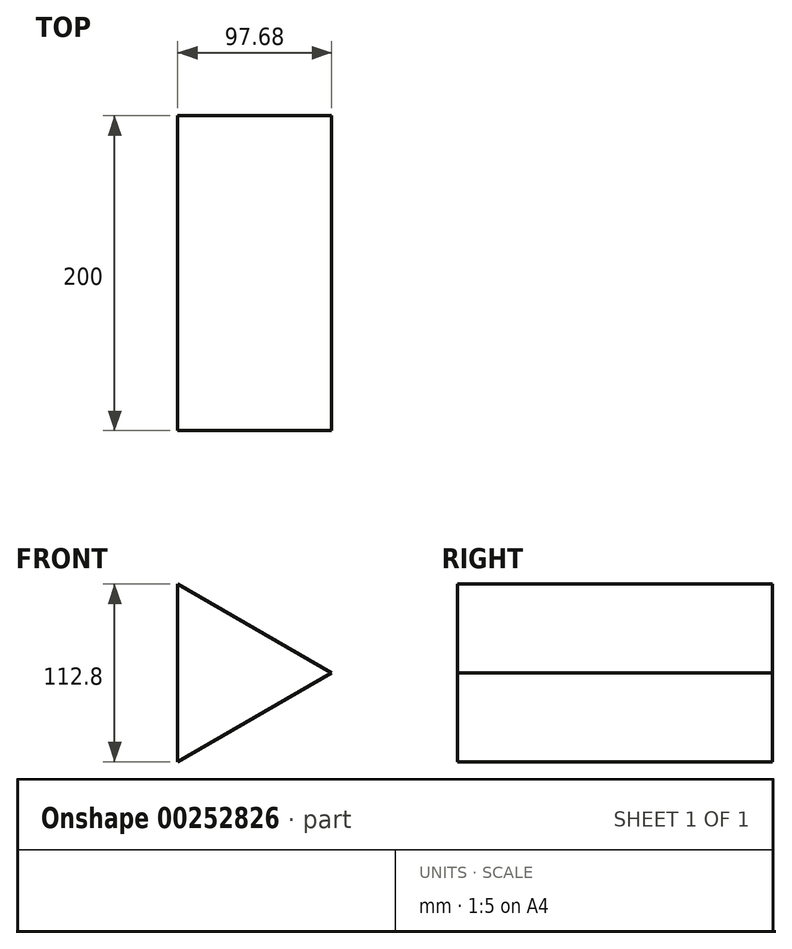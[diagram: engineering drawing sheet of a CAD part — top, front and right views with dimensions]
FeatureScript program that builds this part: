
annotation { "Feature Type Name" : "Feature", "Feature Type Description" : "" }
export const myFeature = defineFeature(function(context is Context, id is Id, definition is map)
    precondition{}
    {
        {
            var Q0;
            Q0=qCreatedBy(makeId("Front.planeOp"),FACE);
            var sketch = newSketch(context, id + "F0", { "sketchPlane" : qUnion([Q0])});
            skCircle(sketch, "E0.cCircle", {"center": v(0, 0) * mm, "radius": 65.12 * mm, "construction": true});
            skLineSegment(sketch, "E0.0", {"start": v(65.12, 0) * mm, "end": v(-32.56, -56.4) * mm});
            skLineSegment(sketch, "E0.1", {"start": v(-32.56, -56.4) * mm, "end": v(-32.56, 56.4) * mm});
            skLineSegment(sketch, "E0.2", {"start": v(-32.56, 56.4) * mm, "end": v(65.12, 0) * mm});
            skSolve(sketch);
        }
        {
            var Q0;
            Q0=makeQuery(id+"F0.imprint","IMPRINT",FACE,{"disambiguationData":[TD([[makeQuery(id+"F0.imprint","IMPRINT",EDGE,{"derivedFrom":sQuery(id+"F0.wireOp",EDGE,"E0.0")}),-1.0]])]});
            extrude(context, id + "F1", {"entities" : qUnion([Q0]), "endBound" : BoundingType.SYMMETRIC, "depth" : 200 * mm});
        }
    });
